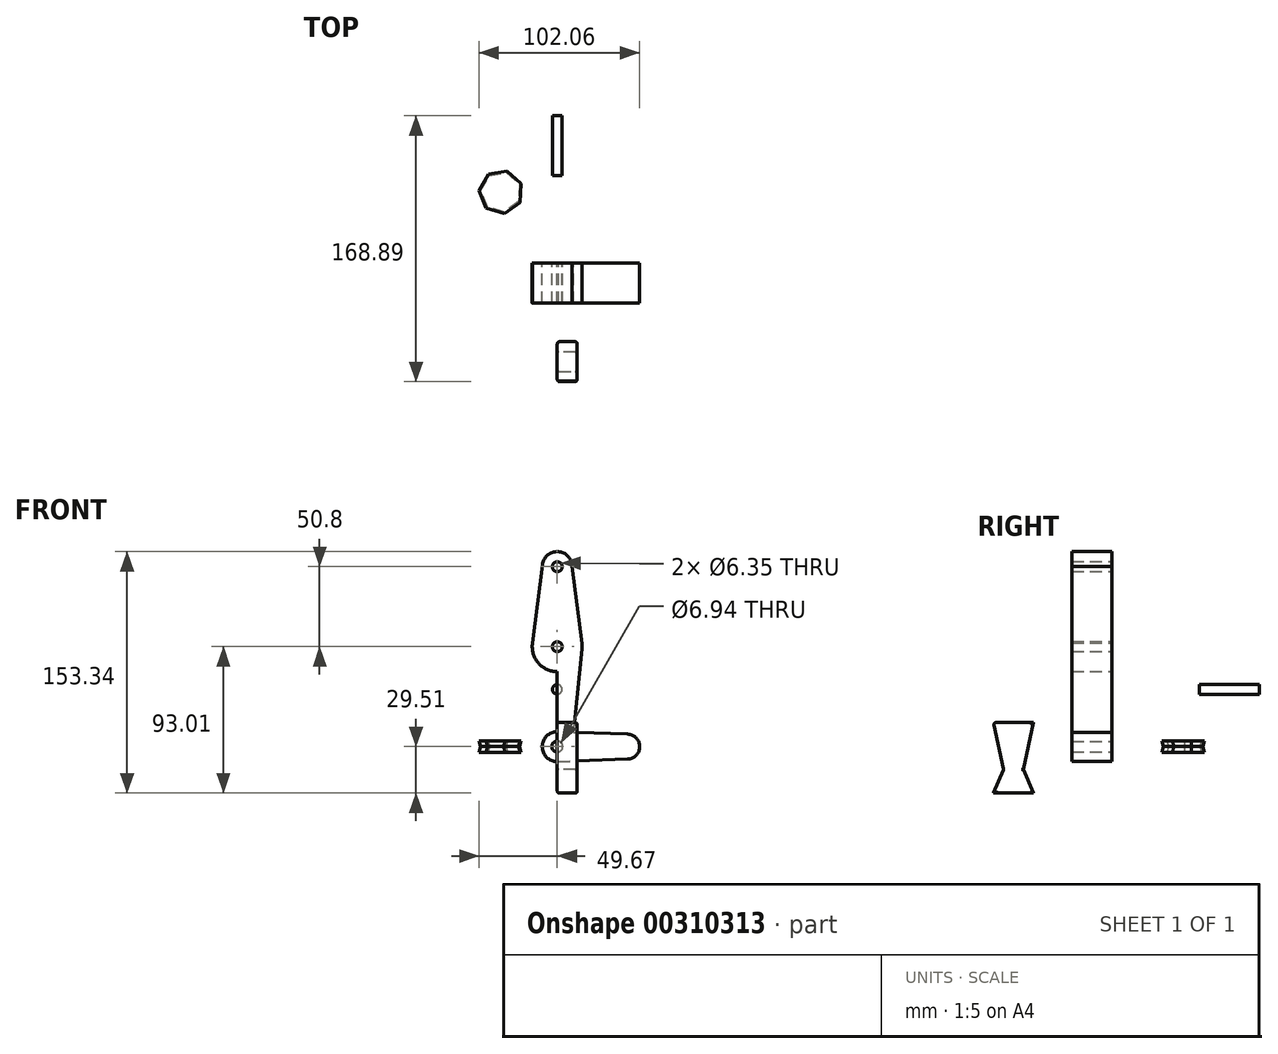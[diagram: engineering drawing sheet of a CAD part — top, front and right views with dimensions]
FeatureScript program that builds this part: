
annotation { "Feature Type Name" : "Feature", "Feature Type Description" : "" }
export const myFeature = defineFeature(function(context is Context, id is Id, definition is map)
    precondition{}
    {
        {
            var Q0;
            Q0=qCreatedBy(makeId("Front.planeOp"),FACE);
            var sketch = newSketch(context, id + "F0", { "sketchPlane" : qUnion([Q0])});
            skLineSegment(sketch, "E0", {"start": v(0, 0) * mm, "end": v(0, 114.3) * mm});
            skLineSegment(sketch, "E1", {"start": v(0, 63.5) * mm, "end": v(0, 114.3) * mm});
            skLineSegment(sketch, "E2", {"start": v(0, 0) * mm, "end": v(44.45, 0) * mm});
            skCircle(sketch, "E3", {"center": v(0, 0) * mm, "radius": 9.53 * mm});
            skCircle(sketch, "E4", {"center": v(44.45, 0) * mm, "radius": 7.94 * mm});
            skCircle(sketch, "E5", {"center": v(0, 114.3) * mm, "radius": 9.53 * mm});
            skCircle(sketch, "E6", {"center": v(0, 63.5) * mm, "radius": 15.88 * mm});
            skLineSegment(sketch, "E7", {"start": v(-9.45, 115.5) * mm, "end": v(-15.8, 65.09) * mm});
            skLineSegment(sketch, "E8", {"start": v(9.27, 116.5) * mm, "end": v(15.75, 65.5) * mm});
            skLineSegment(sketch, "E9", {"start": v(-15.8, 61.91) * mm, "end": v(-9.57, 0) * mm});
            skLineSegment(sketch, "E10", {"start": v(9.52, 0) * mm, "end": v(15.8, 61.9) * mm});
            skLineSegment(sketch, "E11", {"start": v(0, -9.53) * mm, "end": v(44.73, -7.93) * mm});
            skLineSegment(sketch, "E12", {"start": v(0, 9.53) * mm, "end": v(44.73, 7.93) * mm});
            skCircle(sketch, "E13", {"center": v(0, 114.3) * mm, "radius": 3.18 * mm});
            skCircle(sketch, "E14", {"center": v(0, 63.5) * mm, "radius": 3.18 * mm});
            skCircle(sketch, "E15", {"center": v(0, 0) * mm, "radius": 3.47 * mm});
            skSolve(sketch);
        }
        {
            var Q0;
            Q0 = qSketchRegion(id + "F0", true);
            extrude(context, id + "F1", {"entities" : qUnion([Q0]), "depth" : 25.4 * mm});
        }
        {
            var Q0;
            Q0=qCreatedBy(makeId("Top.planeOp"),FACE);
            var sketch = newSketch(context, id + "F2", { "sketchPlane" : qUnion([Q0])});
            skLineSegment(sketch, "E16.0", {"start": v(-24.56, 39.1) * mm, "end": v(-33.67, 32.66) * mm});
            skLineSegment(sketch, "E16.1", {"start": v(-33.67, 32.66) * mm, "end": v(-44.37, 35.78) * mm});
            skLineSegment(sketch, "E16.2", {"start": v(-44.37, 35.78) * mm, "end": v(-48.61, 46.09) * mm});
            skLineSegment(sketch, "E16.3", {"start": v(-48.61, 46.09) * mm, "end": v(-43.2, 55.83) * mm});
            skLineSegment(sketch, "E16.4", {"start": v(-43.2, 55.83) * mm, "end": v(-32.2, 57.67) * mm});
            skLineSegment(sketch, "E16.5", {"start": v(-32.2, 57.67) * mm, "end": v(-23.9, 50.22) * mm});
            skLineSegment(sketch, "E16.6", {"start": v(-23.9, 50.22) * mm, "end": v(-24.56, 39.1) * mm});
            skPoint(sketch, "E16.0.midPoint", {"position": v(-29.11, 35.88) * mm});
            skCircle(sketch, "E17", {"center": v(-35.79, 45.34) * mm, "radius": 4.94 * mm});
            skSolve(sketch);
        }
        {
            var Q0;
            Q0=makeQuery(id+"F2.imprint","IMPRINT",FACE,{"disambiguationData":[TD([[makeQuery(id+"F2.imprint","IMPRINT",EDGE,{"derivedFrom":sQuery(id+"F2.wireOp",EDGE,"E16.0")}),-1.0]])]});
            var Q1;
            Q1=makeQuery(id+"F2.imprint","IMPRINT",FACE,{"disambiguationData":[TD([[makeQuery(id+"F2.imprint","IMPRINT",EDGE,{"derivedFrom":sQuery(id+"F2.wireOp",EDGE,"E17")}),1.0]])]});
            var Q2;
            Q2=sQuery(id+"F2.wireOp",EDGE,"E16.2");
            var Q3;
            Q3=sQuery(id+"F2.wireOp",EDGE,"E16.3");
            var Q4;
            Q4=sQuery(id+"F2.wireOp",EDGE,"E16.4");
            var Q5;
            Q5=sQuery(id+"F2.wireOp",EDGE,"E16.5");
            var Q6;
            Q6=sQuery(id+"F2.wireOp",EDGE,"E16.6");
            var Q7;
            Q7=sQuery(id+"F2.wireOp",EDGE,"E16.0");
            var Q8;
            Q8=sQuery(id+"F2.wireOp",EDGE,"E16.1");
            extrude(context, id + "F3", {"entities" : qUnion([Q0, Q1]), "surfaceEntities" : qUnion([Q2, Q3, Q4, Q5, Q6, Q7, Q8]), "endBound" : BoundingType.SYMMETRIC, "depth" : 7.11 * mm, "hasDraft" : true, "draftAngle" : 15 * degree});
        }
        {
            var Q0;
            Q0=makeQuery(id+"F2.imprint","IMPRINT",FACE,{"disambiguationData":[TD([[makeQuery(id+"F2.imprint","IMPRINT",EDGE,{"derivedFrom":sQuery(id+"F2.wireOp",EDGE,"E17")}),1.0]])]});
            var Q1;
            Q1=sQuery(id+"F2.wireOp",EDGE,"E17");
            extrude(context, id + "F4", {"entities" : qUnion([Q0]), "bodyType" : ToolBodyType.SURFACE, "surfaceEntities" : qUnion([Q1]), "oppositeDirection" : true, "depth" : 7.62 * mm, "hasDraft" : true, "draftAngle" : 40 * degree, "draftPullDirection" : true});
        }
        {
            var Q0;
            Q0=qCreatedBy(makeId("Right.planeOp"),FACE);
            var sketch = newSketch(context, id + "F5", { "sketchPlane" : qUnion([Q0])});
            skLineSegment(sketch, "E18.bottom", {"start": v(-75.21, 15.32) * mm, "end": v(-49.81, 15.32) * mm});
            skLineSegment(sketch, "E18.top", {"start": v(-75.21, -29.51) * mm, "end": v(-49.81, -29.51) * mm});
            skLineSegment(sketch, "E19", {"start": v(-75.21, -29.51) * mm, "end": v(-68.84, -14.48) * mm});
            skLineSegment(sketch, "E20", {"start": v(-68.84, -14.48) * mm, "end": v(-75.21, 15.32) * mm});
            skLineSegment(sketch, "E21", {"start": v(-49.81, 15.32) * mm, "end": v(-56.2, -14.48) * mm});
            skLineSegment(sketch, "E22", {"start": v(-56.2, -14.48) * mm, "end": v(-49.81, -29.51) * mm});
            skLineSegment(sketch, "E23", {"start": v(-62.51, 15.32) * mm, "end": v(-62.51, -29.51) * mm});
            skSolve(sketch);
        }
        {
            var Q0;
            {var subQ0=sQuery(id+"F5.wireOp",EDGE,"E19");Q0=makeQuery(id+"F5.imprint","IMPRINT",FACE,{"disambiguationData":[TD([[makeQuery(id+"F5.imprint","IMPRINT",EDGE,{"derivedFrom":subQ0}),-1.0]])]});}
            var Q1;
            {var subQ3=sQuery(id+"F5.wireOp",EDGE,"E21");Q1=makeQuery(id+"F5.imprint","IMPRINT",FACE,{"disambiguationData":[TD([[makeQuery(id+"F5.imprint","IMPRINT",EDGE,{"derivedFrom":subQ3}),-1.0]])]});}
            extrude(context, id + "F6", {"entities" : qUnion([Q0, Q1]), "depth" : 12.7 * mm});
        }
        {
            var Q0;
            Q0=makeQuery(id+"F6.opExtrude","CAP_FACE",FACE,{"disambiguationData":[OSD([sQuery(id+"F5.wireOp",EDGE,"E18.bottom"),sQuery(id+"F5.wireOp",EDGE,"E18.top"),sQuery(id+"F5.wireOp",EDGE,"E19"),sQuery(id+"F5.wireOp",EDGE,"E20"),sQuery(id+"F5.wireOp",EDGE,"E21"),sQuery(id+"F5.wireOp",EDGE,"E22")])],"isStart":false});
            var Q1;
            Q1=makeQuery(id+"F6.opExtrude","SWEPT_FACE",FACE,{"disambiguationData":[OSD([sQuery(id+"F5.wireOp",EDGE,"E20")])]});
            fillet(context, id + "F7", {"entities" : qUnion([Q0, Q1]), "radius" : 1.27 * mm, "tangentPropagation" : true, "allowEdgeOverflow" : false});
        }
        {
            var Q0;
            Q0=makeQuery(id+"F6.opExtrude","CAP_FACE",FACE,{"disambiguationData":[OSD([sQuery(id+"F5.wireOp",EDGE,"E18.bottom"),sQuery(id+"F5.wireOp",EDGE,"E18.top"),sQuery(id+"F5.wireOp",EDGE,"E19"),sQuery(id+"F5.wireOp",EDGE,"E20"),sQuery(id+"F5.wireOp",EDGE,"E21"),sQuery(id+"F5.wireOp",EDGE,"E22")])],"isStart":true});
            fillet(context, id + "F8", {"entities" : qUnion([Q0]), "radius" : 1.27 * mm, "tangentPropagation" : true, "allowEdgeOverflow" : false});
        }
        {
            var Q0;
            Q0=qCreatedBy(makeId("Right.planeOp"),FACE);
            var sketch = newSketch(context, id + "F9", { "sketchPlane" : qUnion([Q0])});
            skLineSegment(sketch, "E24.bottom", {"start": v(55.58, 36.37) * mm, "end": v(93.68, 36.37) * mm});
            skLineSegment(sketch, "E24.top", {"start": v(55.58, 33.32) * mm, "end": v(93.68, 33.32) * mm});
            skLineSegment(sketch, "E24.left", {"start": v(55.58, 36.37) * mm, "end": v(55.58, 33.32) * mm});
            skLineSegment(sketch, "E24.right", {"start": v(93.68, 36.37) * mm, "end": v(93.68, 33.32) * mm});
            skPoint(sketch, "E25", {"position": v(74.63, 36.37) * mm});
            skSolve(sketch);
        }
        {
            var Q0;
            Q0=makeQuery(id+"F9.imprint","IMPRINT",FACE,{"disambiguationData":[TD([[makeQuery(id+"F9.imprint","IMPRINT",EDGE,{"derivedFrom":sQuery(id+"F9.wireOp",EDGE,"E24.bottom")}),-1.0]])]});
            var Q1;
            Q1=sQuery(id+"F9.wireOp",EDGE,"E24.bottom");
            revolve(context, id + "F10", {"entities" : qUnion([Q0]), "axis" : qUnion([Q1]), "revolveType" : RevolveType.FULL});
        }
    });
